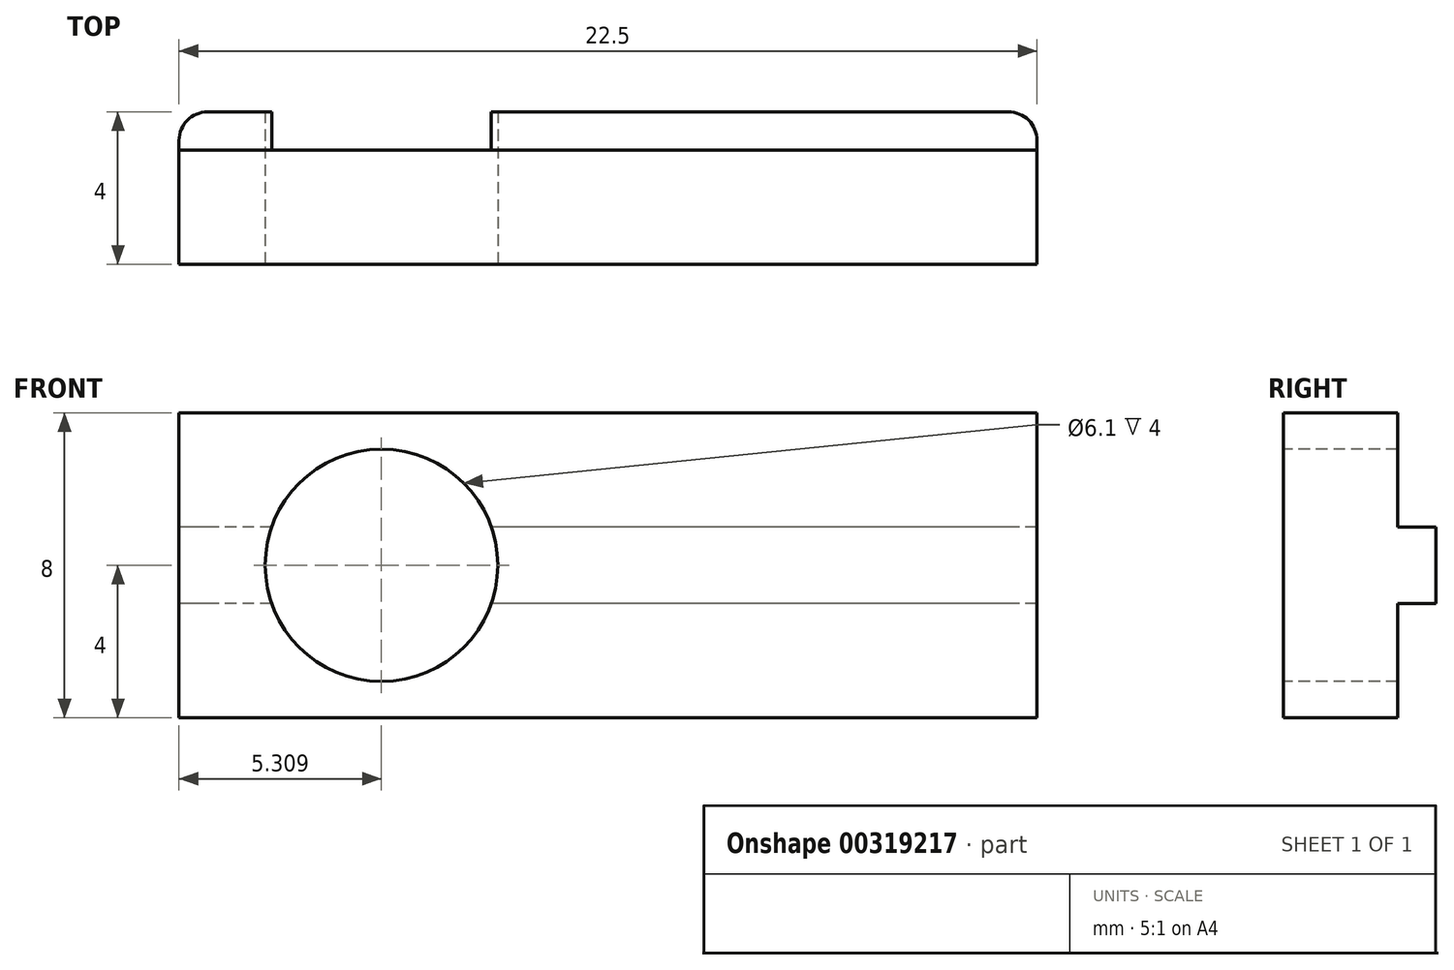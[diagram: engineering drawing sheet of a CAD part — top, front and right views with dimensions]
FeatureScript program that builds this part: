
annotation { "Feature Type Name" : "Feature", "Feature Type Description" : "" }
export const myFeature = defineFeature(function(context is Context, id is Id, definition is map)
    precondition{}
    {
        {
            var Q0;
            Q0=qCreatedBy(makeId("Front.planeOp"),FACE);
            var sketch = newSketch(context, id + "F0", { "sketchPlane" : qUnion([Q0])});
            skLineSegment(sketch, "E0.bottom", {"start": v(-11.25, 4) * mm, "end": v(11.25, 4) * mm});
            skLineSegment(sketch, "E0.top", {"start": v(-11.25, -4) * mm, "end": v(11.25, -4) * mm});
            skLineSegment(sketch, "E0.left", {"start": v(-11.25, 4) * mm, "end": v(-11.25, -4) * mm});
            skLineSegment(sketch, "E0.right", {"start": v(11.25, 4) * mm, "end": v(11.25, -4) * mm});
            skPoint(sketch, "E0.middle", {"position": v(0, 0) * mm});
            skSolve(sketch);
        }
        {
            var Q0;
            Q0=qCreatedBy(makeId("Front.planeOp"),FACE);
            var sketch = newSketch(context, id + "F1", { "sketchPlane" : qUnion([Q0])});
            skLineSegment(sketch, "E1.bottom", {"start": v(11.25, 1) * mm, "end": v(-11.25, 1) * mm});
            skLineSegment(sketch, "E1.top", {"start": v(11.25, -1) * mm, "end": v(-11.25, -1) * mm});
            skLineSegment(sketch, "E1.left", {"start": v(11.25, 1) * mm, "end": v(11.25, -1) * mm});
            skLineSegment(sketch, "E1.right", {"start": v(-11.25, 1) * mm, "end": v(-11.25, -1) * mm});
            skPoint(sketch, "E1.middle", {"position": v(0, 0) * mm});
            skSolve(sketch);
        }
        {
            var Q0;
            Q0=makeQuery(id+"F0.imprint","IMPRINT",FACE,{"disambiguationData":[TD([[makeQuery(id+"F0.imprint","IMPRINT",EDGE,{"derivedFrom":sQuery(id+"F0.wireOp",EDGE,"E0.bottom")}),-1.0]])]});
            extrude(context, id + "F2", {"entities" : qUnion([Q0]), "depth" : 3 * mm});
        }
        {
            var Q0;
            Q0=makeQuery(id+"F1.imprint","IMPRINT",FACE,{"disambiguationData":[TD([[makeQuery(id+"F1.imprint","IMPRINT",EDGE,{"derivedFrom":sQuery(id+"F1.wireOp",EDGE,"E1.bottom")}),1.0]])]});
            extrude(context, id + "F3", {"entities" : qUnion([Q0]), "operationType" : NewBodyOperationType.ADD, "oppositeDirection" : true, "depth" : 1 * mm});
        }
        {
            var Q0;
            Q0=makeQuery(id+"F2.opExtrude","CAP_FACE",FACE,{"disambiguationData":[OSD([sQuery(id+"F0.wireOp",EDGE,"E0.bottom"),sQuery(id+"F0.wireOp",EDGE,"E0.top"),sQuery(id+"F0.wireOp",EDGE,"E0.left"),sQuery(id+"F0.wireOp",EDGE,"E0.right")])],"isStart":false});
            var sketch = newSketch(context, id + "F4", { "sketchPlane" : qUnion([Q0])});
            skPoint(sketch, "E2", {"position": v(-5.94, 0) * mm});
            skSolve(sketch);
        }
        {
            var Q0;
            Q0=sQuery(id+"F4.wireOp",VERTEX,"E2");
            var Q1;
            Q1=makeQuery(id+"F2.opExtrude","SWEPT_BODY",BODY,{"disambiguationData":[OSD([sQuery(id+"F0.wireOp",EDGE,"E0.bottom"),sQuery(id+"F0.wireOp",EDGE,"E0.top"),sQuery(id+"F0.wireOp",EDGE,"E0.left"),sQuery(id+"F0.wireOp",EDGE,"E0.right")])]});
            hole(context, id + "F5", {"style" : HoleStyle.SIMPLE, "endStyle" : HoleEndStyle.THROUGH, "holeDiameter" : 6.1 * mm, "isTappedThrough" : true, "tappedDepth" : 12 * mm, "tapClearance" : 3, "locations" : qUnion([Q0]), "scope" : qUnion([Q1])});
        }
        {
            var Q0;
            Q0=makeQuery(id+"F3.opExtrude","CAP_EDGE",EDGE,{"disambiguationData":[OSD([sQuery(id+"F1.wireOp",EDGE,"E1.right")])],"isStart":false});
            fillet(context, id + "F6", {"entities" : qUnion([Q0]), "radius" : 0.75 * mm, "tangentPropagation" : true, "allowEdgeOverflow" : false});
        }
        {
            var Q0;
            Q0=makeQuery(id+"F3.opExtrude","CAP_EDGE",EDGE,{"disambiguationData":[OSD([sQuery(id+"F1.wireOp",EDGE,"E1.left")])],"isStart":false});
            fillet(context, id + "F7", {"entities" : qUnion([Q0]), "radius" : 0.75 * mm, "tangentPropagation" : true, "allowEdgeOverflow" : false});
        }
    });
